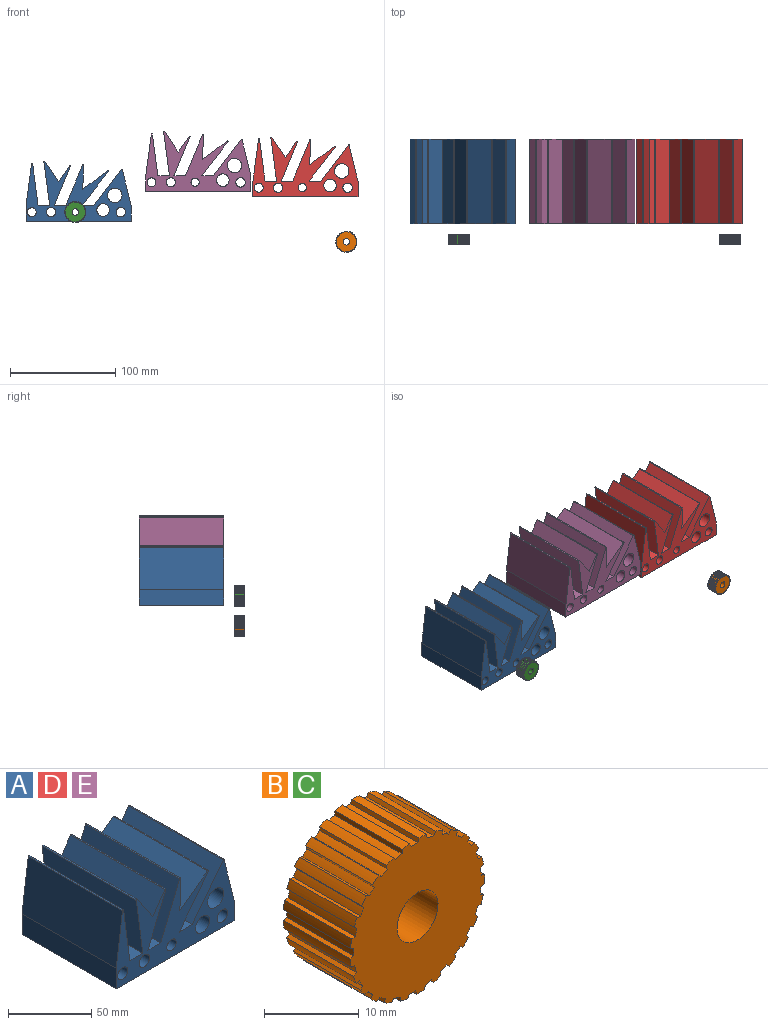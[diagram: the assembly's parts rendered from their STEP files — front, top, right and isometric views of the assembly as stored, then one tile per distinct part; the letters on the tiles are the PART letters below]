
ASSEMBLY  parts=5 mates=3
PART A: 32 faces, bbox 100x80x57 mm
  f0: plane 80x39.76mm, normal (-0.99,0,0.13), area 3208.9mm2, adj f1,f18,f19,f26
  f1: plane 80x15mm, normal (-1,0,0), area 1200mm2, adj f0,f2,f18,f19
  f2: plane 100x80mm, normal (0,0,-1), area 8000mm2, adj f1,f3,f18,f19
  f3: plane 80x15mm, normal (1,0,0), area 1200mm2, adj f2,f4,f18,f19
  f4: plane 80x34.16mm, normal (0.97,0,0.24), area 2813.6mm2, adj f3,f18,f19,f29
  f5: plane 80x34.35mm, normal (-0.79,0,0.61), area 3463.6mm2, adj f6,f18,f19,f29
  f6: plane 80x11mm, normal (0,0,1), area 880mm2, adj f5,f7,f18,f19
  f7: plane 80x32.32mm, normal (0.79,0,-0.61), area 3259.4mm2, adj f6,f18,f19,f28
  f8: plane 80x23.5mm, normal (-0.6,0,0.8), area 2343.3mm2, adj f9,f18,f19,f28
  f9: plane 80x23.24mm, normal (1,0,-0.04), area 1860.4mm2, adj f8,f18,f19,f27
  f10: plane 80x38.99mm, normal (-0.92,0,0.38), area 3376mm2, adj f11,f18,f19,f27
  f11: plane 80x11mm, normal (0,0,1), area 880mm2, adj f10,f12,f18,f19
  f12: plane 80x37.14mm, normal (0.92,0,-0.38), area 3216.3mm2, adj f11,f18,f19,f30
  f13: plane 80x15.02mm, normal (-0.83,0,0.56), area 1456.6mm2, adj f14,f18,f19,f30
  f14: plane 80x19.17mm, normal (0.83,0,0.56), area 1855.7mm2, adj f13,f18,f19,f31
  f15: plane 80x41.42mm, normal (-0.99,0,-0.13), area 3342mm2, adj f16,f18,f19,f31
  f16: plane 80x11mm, normal (0,0,1), area 880mm2, adj f15,f17,f18,f19
  f17: plane 80x39.76mm, normal (0.99,0,0.13), area 3208.1mm2, adj f16,f18,f19,f26
  f18: plane 100x56.98mm, normal (0,-1,0), area 2806.6mm2, adj f0,f1,f2,f3,f4,f5,f6,f7
  f19: plane 100x56.98mm, normal (0,1,0), area 2806.6mm2, adj f0,f1,f2,f3,f4,f5,f6,f7
  f20: cylinder r=5.99mm len=80mm, axis (0,1,0), area 3010.8mm2, adj f18,f19
  f21: cylinder r=3.94mm len=80mm, axis (0,1,0), area 1982.1mm2, adj f18,f19
  f22: cylinder r=6.89mm len=80mm, axis (0,1,0), area 3463.9mm2, adj f18,f19
  f23: cylinder r=4.38mm len=80mm, axis (0,1,0), area 2200.7mm2, adj f18,f19
  f24: cylinder r=4.5mm len=80mm, axis (0,1,0), area 2260.2mm2, adj f18,f19
  f25: cylinder r=4.25mm len=80mm, axis (0,1,0), area 2137.5mm2, adj f18,f19
  f26: cylinder r=0.5mm len=80mm, axis (0,-1,0), area 115.1mm2, adj f0,f17,f18,f19
  f27: cylinder r=0.5mm len=80mm, axis (0,1,0), area 111.5mm2, adj f9,f10,f18,f19
  f28: cylinder r=0.5mm len=80mm, axis (0,-1,0), area 114.6mm2, adj f7,f8,f18,f19
  f29: cylinder r=0.5mm len=80mm, axis (0,1,0), area 89.9mm2, adj f4,f5,f18,f19
  f30: cylinder r=0.5mm len=80mm, axis (0,1,0), area 117.4mm2, adj f12,f13,f18,f19
  f31: cylinder r=0.5mm len=80mm, axis (0,1,0), area 107mm2, adj f14,f15,f18,f19
PART B: 103 faces, bbox 20x10x20 mm
  f0: plane 10x0.49mm, normal (0.95,0,0.32), area 5.2mm2, adj f1,f99,f100,f101
  f1: cylinder r=9.5mm len=10mm, axis (0,1,0), area 10mm2, adj f0,f2,f100,f101
  f2: plane 10x0.45mm, normal (-0.52,0,-0.85), area 5.2mm2, adj f1,f3,f100,f101
  f3: cylinder r=10mm len=10mm, axis (0,1,0), area 11.6mm2, adj f2,f4,f100,f101
  f4: plane 10x0.44mm, normal (0.84,0,0.55), area 5.2mm2, adj f3,f5,f100,f101
  f5: cylinder r=9.5mm len=10mm, axis (0,1,0), area 10mm2, adj f4,f6,f100,f101
  f6: plane 10x0.5mm, normal (-0.29,0,-0.96), area 5.2mm2, adj f5,f7,f100,f101
  f7: cylinder r=10mm len=10mm, axis (0,1,0), area 11.6mm2, adj f6,f8,f100,f101
  f8: plane 10x0.38mm, normal (0.68,0,0.74), area 5.2mm2, adj f7,f9,f100,f101
  f9: cylinder r=9.5mm len=10mm, axis (0,1,0), area 10mm2, adj f8,f10,f100,f101
  f10: plane 10x0.52mm, normal (-0.04,0,-1), area 5.2mm2, adj f9,f11,f100,f101
  f11: cylinder r=10mm len=10mm, axis (0,1,0), area 11.6mm2, adj f10,f12,f100,f101
  f12: plane 10x0.46mm, normal (0.47,0,0.88), area 5.2mm2, adj f11,f13,f100,f101
  f13: cylinder r=9.5mm len=10mm, axis (0,1,0), area 10mm2, adj f12,f14,f100,f101
  f14: plane 10x0.51mm, normal (0.21,0,-0.98), area 5.2mm2, adj f13,f15,f100,f101
  f15: cylinder r=10mm len=10mm, axis (0,1,0), area 11.6mm2, adj f14,f16,f100,f101
  f16: plane 10x0.51mm, normal (0.24,0,0.97), area 5.2mm2, adj f15,f17,f100,f101
  f17: cylinder r=9.5mm len=10mm, axis (0,1,0), area 10mm2, adj f16,f18,f100,f101
  f18: plane 10x0.47mm, normal (0.44,0,-0.9), area 5.2mm2, adj f17,f19,f100,f101
  f19: cylinder r=10mm len=10mm, axis (0,1,0), area 11.6mm2, adj f18,f20,f100,f101
  f20: plane 10x0.52mm, normal (-0.01,0,1), area 5.2mm2, adj f19,f21,f100,f101
  f21: cylinder r=9.5mm len=10mm, axis (0,1,0), area 10mm2, adj f20,f22,f100,f101
  f22: plane 10x0.4mm, normal (0.65,0,-0.76), area 5.2mm2, adj f21,f23,f100,f101
  f23: cylinder r=10mm len=10mm, axis (0,1,0), area 11.6mm2, adj f22,f24,f100,f101
  f24: plane 10x0.5mm, normal (-0.26,0,0.97), area 5.2mm2, adj f23,f25,f100,f101
  f25: cylinder r=9.5mm len=10mm, axis (0,1,0), area 10mm2, adj f24,f26,f100,f101
  f26: plane 10x0.43mm, normal (0.82,0,-0.57), area 5.2mm2, adj f25,f27,f100,f101
  f27: cylinder r=10mm len=10mm, axis (0,1,0), area 11.6mm2, adj f26,f28,f100,f101
  f28: plane 10x0.45mm, normal (-0.49,0,0.87), area 5.2mm2, adj f27,f29,f100,f101
  f29: cylinder r=9.5mm len=10mm, axis (0,1,0), area 10mm2, adj f28,f30,f100,f101
  f30: plane 10x0.49mm, normal (0.94,0,-0.35), area 5.2mm2, adj f29,f31,f100,f101
  f31: cylinder r=10mm len=10mm, axis (0,1,0), area 11.6mm2, adj f30,f32,f100,f101
  f32: plane 10x0.38mm, normal (-0.69,0,0.72), area 5.2mm2, adj f31,f33,f100,f101
  f33: cylinder r=9.5mm len=10mm, axis (0,1,0), area 10mm2, adj f32,f34,f100,f101
  f34: plane 10x0.52mm, normal (0.99,0,-0.11), area 5.2mm2, adj f33,f35,f100,f101
  f35: cylinder r=10mm len=10mm, axis (0,1,0), area 11.6mm2, adj f34,f36,f100,f101
  f36: plane 10x0.44mm, normal (-0.85,0,0.53), area 5.2mm2, adj f35,f37,f100,f101
  f37: cylinder r=9.5mm len=10mm, axis (0,1,0), area 10mm2, adj f36,f38,f100,f101
  f38: plane 10x0.52mm, normal (0.99,0,0.14), area 5.2mm2, adj f37,f39,f100,f101
  f39: cylinder r=10mm len=10mm, axis (0,1,0), area 11.6mm2, adj f38,f40,f100,f101
  f40: plane 10x0.5mm, normal (-0.95,0,0.3), area 5.2mm2, adj f39,f41,f100,f101
  f41: cylinder r=9.5mm len=10mm, axis (0,1,0), area 10mm2, adj f40,f42,f100,f101
  f42: plane 10x0.48mm, normal (0.92,0,0.39), area 5.2mm2, adj f41,f43,f100,f101
  f43: cylinder r=10mm len=10mm, axis (0,1,0), area 11.6mm2, adj f42,f44,f100,f101
  f44: plane 10x0.52mm, normal (-1,0,0.05), area 5.2mm2, adj f43,f45,f100,f101
  f45: cylinder r=9.5mm len=10mm, axis (0,1,0), area 10mm2, adj f44,f46,f100,f101
  f46: plane 10x0.42mm, normal (0.8,0,0.6), area 5.2mm2, adj f45,f47,f100,f101
  f47: cylinder r=10mm len=10mm, axis (0,1,0), area 11.6mm2, adj f46,f48,f100,f101
  f48: plane 10x0.51mm, normal (-0.98,0,-0.2), area 5.2mm2, adj f47,f49,f100,f101
  f49: cylinder r=9.5mm len=10mm, axis (0,1,0), area 10mm2, adj f48,f50,f100,f101
  f50: plane 10x0.41mm, normal (0.62,0,0.78), area 5.2mm2, adj f49,f51,f100,f101
  f51: cylinder r=10mm len=10mm, axis (0,1,0), area 11.6mm2, adj f50,f52,f100,f101
  f52: plane 10x0.47mm, normal (-0.9,0,-0.44), area 5.2mm2, adj f51,f53,f100,f101
  f53: cylinder r=9.5mm len=10mm, axis (0,1,0), area 10mm2, adj f52,f54,f100,f101
  f54: plane 10x0.48mm, normal (0.41,0,0.91), area 5.2mm2, adj f53,f55,f100,f101
  f55: cylinder r=10mm len=10mm, axis (0,1,0), area 11.6mm2, adj f54,f56,f100,f101
  f56: plane 10x0.4mm, normal (-0.76,0,-0.65), area 5.2mm2, adj f55,f57,f100,f101
  f57: cylinder r=9.5mm len=10mm, axis (0,1,0), area 10mm2, adj f56,f58,f100,f101
  f58: plane 10x0.51mm, normal (0.17,0,0.99), area 5.2mm2, adj f57,f59,f100,f101
  f59: cylinder r=10mm len=10mm, axis (0,1,0), area 11.6mm2, adj f58,f60,f100,f101
  f60: plane 10x0.43mm, normal (-0.58,0,-0.82), area 5.2mm2, adj f59,f61,f100,f101
  f61: cylinder r=9.5mm len=10mm, axis (0,1,0), area 10mm2, adj f60,f62,f100,f101
  f62: plane 10x0.52mm, normal (-0.08,0,1), area 5.2mm2, adj f61,f63,f100,f101
  f63: cylinder r=10mm len=10mm, axis (0,1,0), area 11.6mm2, adj f62,f64,f100,f101
  f64: plane 10x0.49mm, normal (-0.36,0,-0.93), area 5.2mm2, adj f63,f65,f100,f101
  f65: cylinder r=9.5mm len=10mm, axis (0,1,0), area 10mm2, adj f64,f66,f100,f101
  f66: plane 10x0.49mm, normal (-0.33,0,0.94), area 5.2mm2, adj f65,f67,f100,f101
  f67: cylinder r=10mm len=10mm, axis (0,1,0), area 11.6mm2, adj f66,f68,f100,f101
  f68: plane 10x0.52mm, normal (-0.11,0,-0.99), area 5.2mm2, adj f67,f69,f100,f101
  f69: cylinder r=9.5mm len=10mm, axis (0,1,0), area 10mm2, adj f68,f70,f100,f101
  f70: plane 10x0.44mm, normal (-0.55,0,0.83), area 5.2mm2, adj f69,f71,f100,f101
  f71: cylinder r=10mm len=10mm, axis (0,1,0), area 11.6mm2, adj f70,f72,f100,f101
  f72: plane 10x0.52mm, normal (0.14,0,-0.99), area 5.2mm2, adj f71,f73,f100,f101
  f73: cylinder r=9.5mm len=10mm, axis (0,1,0), area 10mm2, adj f72,f74,f100,f101
  f74: plane 10x0.39mm, normal (-0.74,0,0.67), area 5.2mm2, adj f73,f75,f100,f101
  f75: cylinder r=10mm len=10mm, axis (0,1,0), area 11.6mm2, adj f74,f76,f100,f101
  f76: plane 10x0.48mm, normal (0.38,0,-0.93), area 5.2mm2, adj f75,f77,f100,f101
  f77: cylinder r=9.5mm len=10mm, axis (0,1,0), area 10mm2, adj f76,f78,f100,f101
  f78: plane 10x0.46mm, normal (-0.89,0,0.46), area 5.2mm2, adj f77,f79,f100,f101
  f79: cylinder r=10mm len=10mm, axis (0,1,0), area 11.6mm2, adj f78,f80,f100,f101
  f80: plane 10x0.42mm, normal (0.6,0,-0.8), area 5.2mm2, adj f79,f81,f100,f101
  f81: cylinder r=9.5mm len=10mm, axis (0,1,0), area 10mm2, adj f80,f82,f100,f101
  f82: plane 10x0.51mm, normal (-0.97,0,0.23), area 5.2mm2, adj f81,f83,f100,f101
  f83: cylinder r=10mm len=10mm, axis (0,1,0), area 11.6mm2, adj f82,f84,f100,f101
  f84: plane 10x0.41mm, normal (0.78,0,-0.63), area 5.2mm2, adj f83,f85,f100,f101
  f85: cylinder r=9.5mm len=10mm, axis (0,1,0), area 10mm2, adj f84,f86,f100,f101
  f86: plane 10x0.52mm, normal (-1,0,-0.02), area 5.2mm2, adj f85,f87,f100,f101
  f87: cylinder r=10mm len=10mm, axis (0,1,0), area 11.6mm2, adj f86,f88,f100,f101
  f88: plane 10x0.47mm, normal (0.91,0,-0.41), area 5.2mm2, adj f87,f89,f100,f101
  f89: cylinder r=9.5mm len=10mm, axis (0,1,0), area 10mm2, adj f88,f90,f100,f101
  f90: plane 10x0.5mm, normal (-0.96,0,-0.27), area 5.2mm2, adj f89,f91,f100,f101
  f91: cylinder r=10mm len=10mm, axis (0,1,0), area 11.6mm2, adj f90,f92,f100,f101
  f92: plane 10x0.51mm, normal (0.98,0,-0.18), area 5.2mm2, adj f91,f93,f100,f101
  f93: cylinder r=9.5mm len=10mm, axis (0,1,0), area 10mm2, adj f92,f94,f100,f101
  f94: plane 10x0.45mm, normal (-0.87,0,-0.5), area 5.2mm2, adj f93,f95,f100,f101
  f95: cylinder r=10mm len=10mm, axis (0,1,0), area 11.6mm2, adj f94,f96,f100,f101
  f96: plane 10x0.52mm, normal (1,0,0.07), area 5.2mm2, adj f95,f97,f100,f101
  f97: cylinder r=9.5mm len=10mm, axis (0,1,0), area 10mm2, adj f96,f98,f100,f101
  f98: plane 10x0.37mm, normal (-0.72,0,-0.7), area 5.2mm2, adj f97,f99,f100,f101
  f99: cylinder r=10mm len=10mm, axis (0,1,0), area 11.6mm2, adj f0,f98,f100,f101
  f100: plane 20x19.99mm, normal (0,-1,0), area 270.2mm2, adj f0,f1,f2,f3,f4,f5,f6,f7
  f101: plane 20x19.99mm, normal (0,1,0), area 270.2mm2, adj f0,f1,f2,f3,f4,f5,f6,f7
  f102: cylinder r=3.05mm len=10mm, axis (0,-1,0), area 191.6mm2, adj f100,f101
PART C: same geometry as B
PART D: same geometry as A
PART E: same geometry as A
PLACE A t=(72.31,181.13,21.72)mm
PLACE B t=(377.25,91.13,2.2)mm
PLACE C t=(119.27,91.13,30.57)mm
PLACE D t=(288.28,181.13,44.98)mm
PLACE E t=(186.28,181.13,50.09)mm
MATE parallel E.f18 <-> A.f29  axis (0,-1,0) through (235.42,101.13,70.76)mm
MATE parallel A.f2 <-> E.f2  axis (0,0,-1) through (172.31,141.13,21.72)mm
MATE fastened C.f102 <-> A.f21  axis (0,1,0) through (119.27,91.13,30.57)mm
